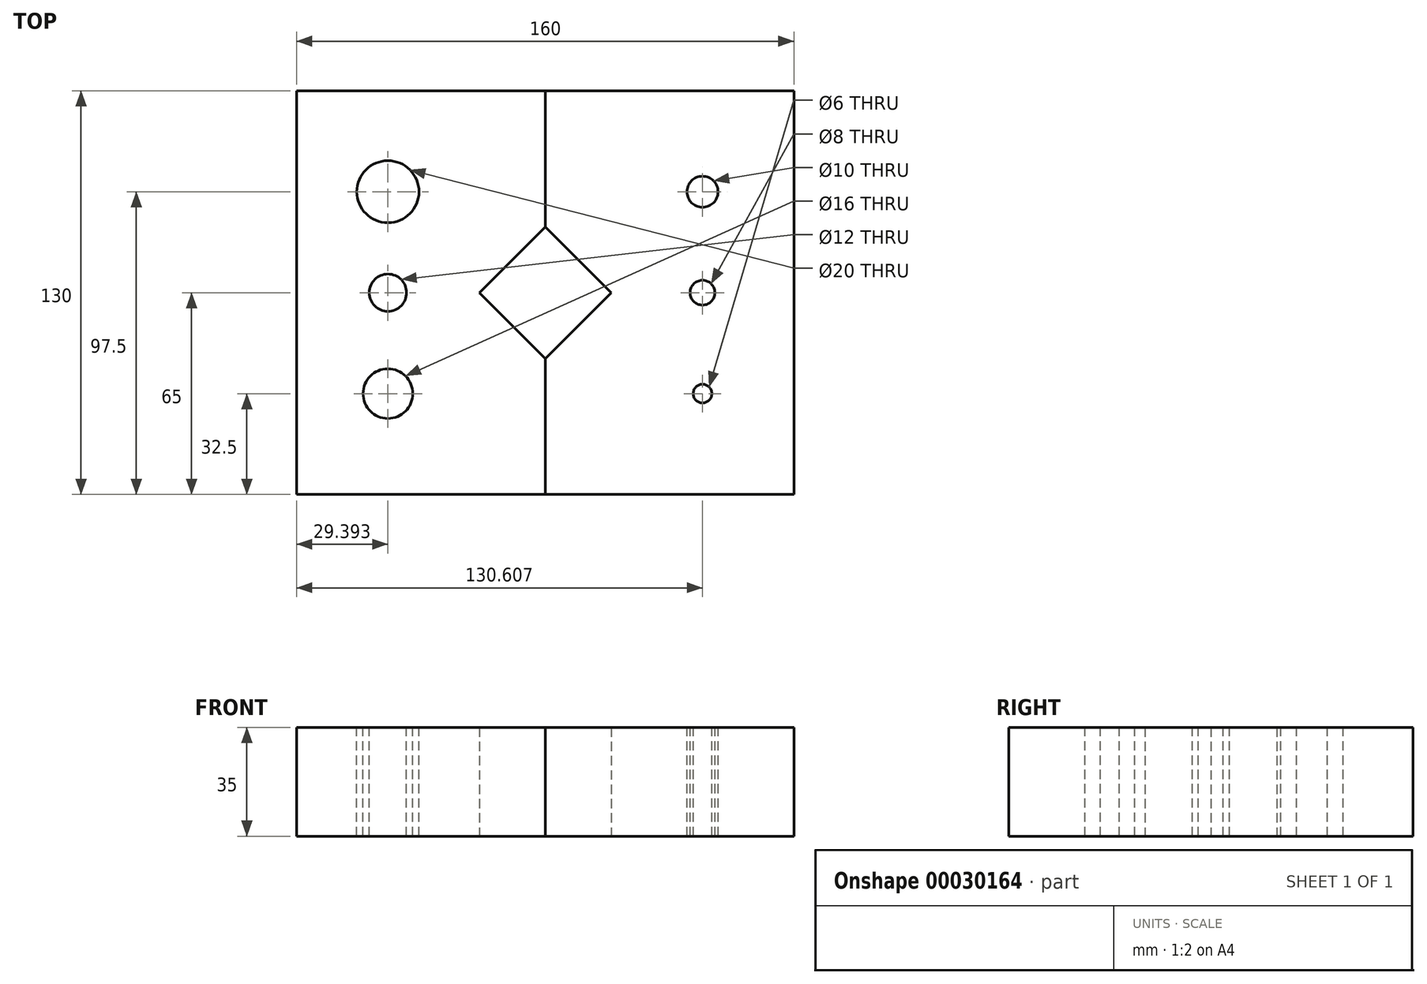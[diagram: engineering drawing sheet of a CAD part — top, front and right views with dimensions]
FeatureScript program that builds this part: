
annotation { "Feature Type Name" : "Feature", "Feature Type Description" : "" }
export const myFeature = defineFeature(function(context is Context, id is Id, definition is map)
    precondition{}
    {
        {
            var Q0;
            Q0=qCreatedBy(makeId("Top.planeOp"),FACE);
            var sketch = newSketch(context, id + "F0", { "sketchPlane" : qUnion([Q0])});
            skLineSegment(sketch, "E0.rect.bottom", {"start": v(80, -65) * mm, "end": v(-80, -65) * mm});
            skLineSegment(sketch, "E0.rect.top", {"start": v(80, 65) * mm, "end": v(-80, 65) * mm});
            skLineSegment(sketch, "E0.rect.left", {"start": v(80, -65) * mm, "end": v(80, 65) * mm});
            skLineSegment(sketch, "E0.rect.right", {"start": v(-80, -65) * mm, "end": v(-80, 65) * mm});
            skPoint(sketch, "E0.rect.middle", {"position": v(0, 0) * mm});
            skLineSegment(sketch, "E1", {"start": v(0, 65) * mm, "end": v(0, -65) * mm});
            skCircle(sketch, "E2", {"center": v(0, 0) * mm, "radius": 15 * mm});
            skCircle(sketch, "E3.cCircle", {"center": v(0, 0) * mm, "radius": 15 * mm, "construction": true});
            skLineSegment(sketch, "E3.0", {"start": v(21.21, 0) * mm, "end": v(0, -21.21) * mm});
            skLineSegment(sketch, "E3.1", {"start": v(0, -21.21) * mm, "end": v(-21.21, 0) * mm});
            skLineSegment(sketch, "E3.2", {"start": v(-21.21, 0) * mm, "end": v(0, 21.21) * mm});
            skLineSegment(sketch, "E3.3", {"start": v(0, 21.21) * mm, "end": v(21.21, 0) * mm});
            skPoint(sketch, "E3.0.midPoint", {"position": v(10.6, -10.6) * mm});
            skSolve(sketch);
        }
        {
            var Q0;
            {var subQ13=sQuery(id+"F0.wireOp",EDGE,"E0.rect.right");Q0=makeQuery(id+"F0.imprint","IMPRINT",FACE,{"disambiguationData":[TD([[makeQuery(id+"F0.imprint","IMPRINT",EDGE,{"derivedFrom":subQ13}),-1.0]])]});}
            extrude(context, id + "F1", {"entities" : qUnion([Q0]), "depth" : 35 * mm});
        }
        {
            var Q0;
            {var subQ13=sQuery(id+"F0.wireOp",EDGE,"E0.rect.left");Q0=makeQuery(id+"F0.imprint","IMPRINT",FACE,{"disambiguationData":[TD([[makeQuery(id+"F0.imprint","IMPRINT",EDGE,{"derivedFrom":subQ13}),1.0]])]});}
            extrude(context, id + "F2", {"entities" : qUnion([Q0]), "depth" : 35 * mm});
        }
        {
            var Q0;
            Q0=makeQuery(id+"F1.opExtrude","CAP_FACE",FACE,{"disambiguationData":[OSD([sQuery(id+"F0.wireOp",EDGE,"E0.rect.bottom"),sQuery(id+"F0.wireOp",EDGE,"E0.rect.top"),sQuery(id+"F0.wireOp",EDGE,"E0.rect.right"),sQuery(id+"F0.wireOp",EDGE,"E1"),sQuery(id+"F0.wireOp",EDGE,"E3.1"),sQuery(id+"F0.wireOp",EDGE,"E3.2")])],"isStart":false});
            var sketch = newSketch(context, id + "F3", { "sketchPlane" : qUnion([Q0])});
            skLineSegment(sketch, "E4", {"start": v(-21.21, 0) * mm, "end": v(-80, 0) * mm, "construction": true});
            skLineSegment(sketch, "E5", {"start": v(-50.6, 0) * mm, "end": v(-50.6, 65) * mm, "construction": true});
            skLineSegment(sketch, "E6", {"start": v(-50.6, 0) * mm, "end": v(-50.6, -65) * mm, "construction": true});
            skCircle(sketch, "E7", {"center": v(-50.6, 32.5) * mm, "radius": 10 * mm});
            skCircle(sketch, "E8", {"center": v(-50.6, -32.5) * mm, "radius": 8 * mm});
            skCircle(sketch, "E9", {"center": v(-50.6, 0) * mm, "radius": 6 * mm});
            skSolve(sketch);
        }
        {
            var Q0;
            Q0=makeQuery(id+"F3.imprint","IMPRINT",FACE,{"disambiguationData":[TD([[makeQuery(id+"F3.imprint","IMPRINT",EDGE,{"derivedFrom":sQuery(id+"F3.wireOp",EDGE,"E7")}),1.0]])]});
            var Q1;
            Q1=makeQuery(id+"F3.imprint","IMPRINT",FACE,{"disambiguationData":[TD([[makeQuery(id+"F3.imprint","IMPRINT",EDGE,{"derivedFrom":sQuery(id+"F3.wireOp",EDGE,"E9")}),1.0]])]});
            var Q2;
            Q2=makeQuery(id+"F3.imprint","IMPRINT",FACE,{"disambiguationData":[TD([[makeQuery(id+"F3.imprint","IMPRINT",EDGE,{"derivedFrom":sQuery(id+"F3.wireOp",EDGE,"E8")}),1.0]])]});
            extrude(context, id + "F4", {"entities" : qUnion([Q0, Q1, Q2]), "operationType" : NewBodyOperationType.REMOVE, "oppositeDirection" : true, "depth" : 35 * mm});
        }
        {
            var Q0;
            Q0=makeQuery(id+"F2.opExtrude","CAP_FACE",FACE,{"disambiguationData":[OSD([sQuery(id+"F0.wireOp",EDGE,"E0.rect.bottom"),sQuery(id+"F0.wireOp",EDGE,"E0.rect.top"),sQuery(id+"F0.wireOp",EDGE,"E0.rect.left"),sQuery(id+"F0.wireOp",EDGE,"E1"),sQuery(id+"F0.wireOp",EDGE,"E3.0"),sQuery(id+"F0.wireOp",EDGE,"E3.3")])],"isStart":false});
            var sketch = newSketch(context, id + "F5", { "sketchPlane" : qUnion([Q0])});
            skLineSegment(sketch, "E10", {"start": v(21.21, 0) * mm, "end": v(80, 0) * mm, "construction": true});
            skLineSegment(sketch, "E11", {"start": v(50.6, 0) * mm, "end": v(50.6, -65) * mm, "construction": true});
            skLineSegment(sketch, "E12", {"start": v(50.6, 0) * mm, "end": v(50.6, 65) * mm, "construction": true});
            skCircle(sketch, "E13", {"center": v(50.6, 32.5) * mm, "radius": 5 * mm});
            skCircle(sketch, "E14", {"center": v(50.6, 0) * mm, "radius": 4 * mm});
            skCircle(sketch, "E15", {"center": v(50.6, -32.5) * mm, "radius": 3 * mm});
            skSolve(sketch);
        }
        {
            var Q0;
            Q0 = qSketchRegion(id + "F5", true);
            extrude(context, id + "F6", {"entities" : qUnion([Q0]), "operationType" : NewBodyOperationType.REMOVE, "oppositeDirection" : true, "depth" : 35 * mm});
        }
    });
